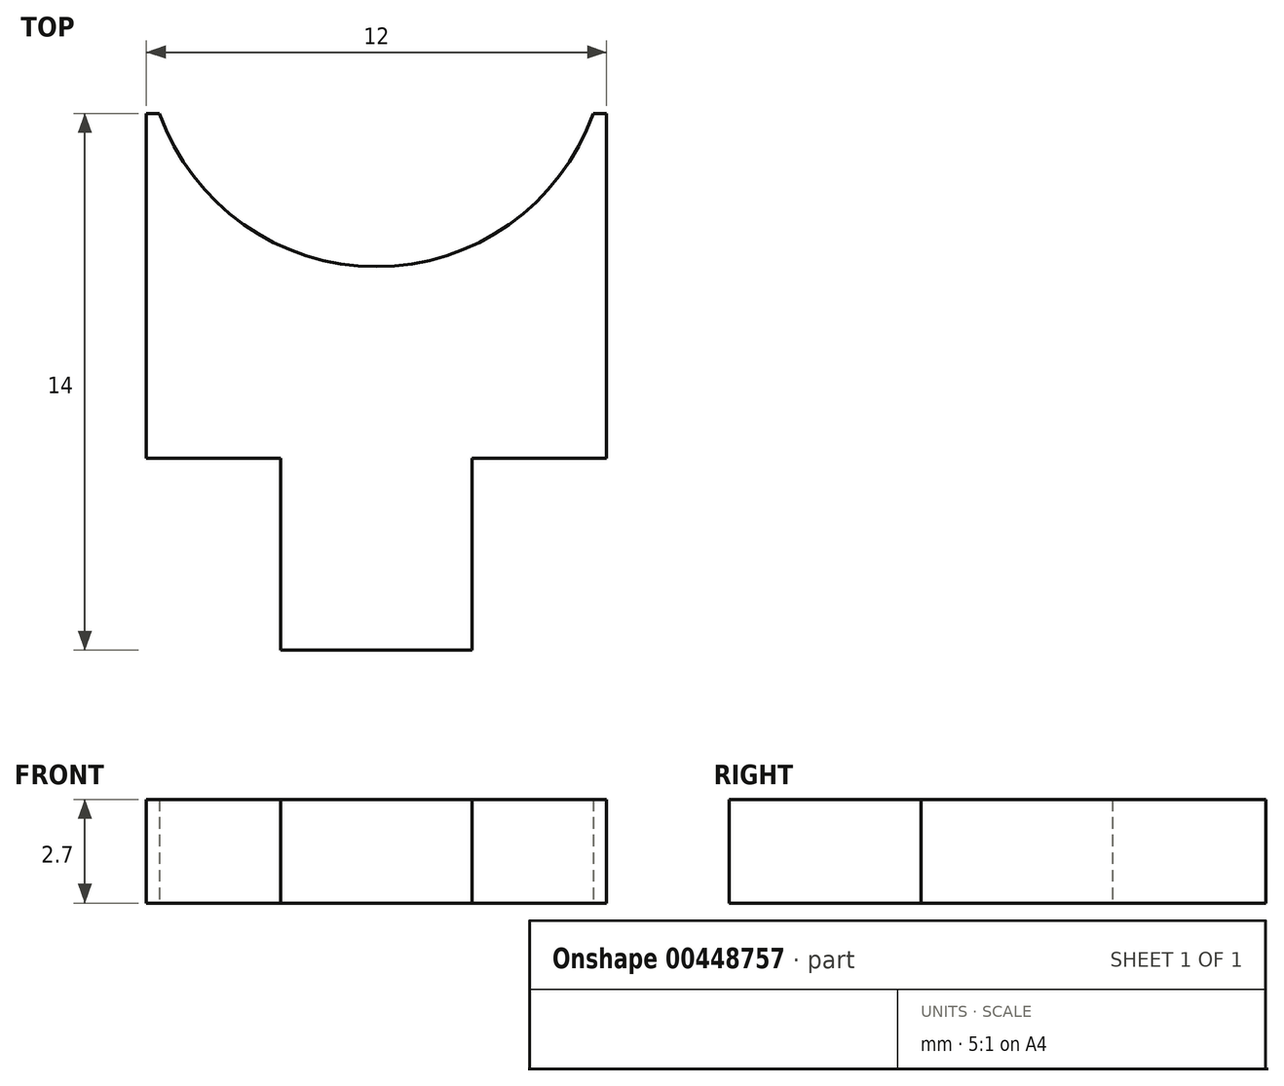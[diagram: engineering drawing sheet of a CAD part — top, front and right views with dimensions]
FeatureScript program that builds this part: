
annotation { "Feature Type Name" : "Feature", "Feature Type Description" : "" }
export const myFeature = defineFeature(function(context is Context, id is Id, definition is map)
    precondition{}
    {
        {
            var Q0;
            Q0=qCreatedBy(makeId("Top.planeOp"),FACE);
            var sketch = newSketch(context, id + "F0", { "sketchPlane" : qUnion([Q0])});
            skLineSegment(sketch, "E0.bottom", {"start": v(6, 4.5) * mm, "end": v(5.66, 4.5) * mm});
            skLineSegment(sketch, "E0.top", {"start": v(6, -4.5) * mm, "end": v(-6, -4.5) * mm});
            skLineSegment(sketch, "E0.left", {"start": v(6, 4.5) * mm, "end": v(6, -4.5) * mm});
            skLineSegment(sketch, "E0.right", {"start": v(-6, 4.5) * mm, "end": v(-6, -4.5) * mm});
            skPoint(sketch, "E0.middle", {"position": v(0, 0) * mm});
            skLineSegment(sketch, "E1", {"start": v(-6, 6.5) * mm, "end": v(6, 6.5) * mm, "construction": true});
            skArc(sketch, "E2", {"start": v(-5.66, 4.5) * mm, "mid": v(0, 0.5) * mm, "end": v(5.66, 4.5) * mm});
            skLineSegment(sketch, "E3.trimOffspring", {"start": v(-5.66, 4.5) * mm, "end": v(-6, 4.5) * mm});
            skLineSegment(sketch, "E4", {"start": v(-2.5, -4.5) * mm, "end": v(-2.5, -9.5) * mm});
            skLineSegment(sketch, "E5", {"start": v(-2.5, -9.5) * mm, "end": v(2.5, -9.5) * mm});
            skLineSegment(sketch, "E6", {"start": v(2.5, -9.5) * mm, "end": v(2.5, -4.5) * mm});
            skPoint(sketch, "E7", {"position": v(0, -9.5) * mm});
            skSolve(sketch);
        }
        {
            var Q0;
            Q0=qSketchRegion(id+"F0",true);
            extrude(context, id + "F1", {"entities" : qUnion([Q0]), "depth" : 2.7 * mm});
        }
    });
